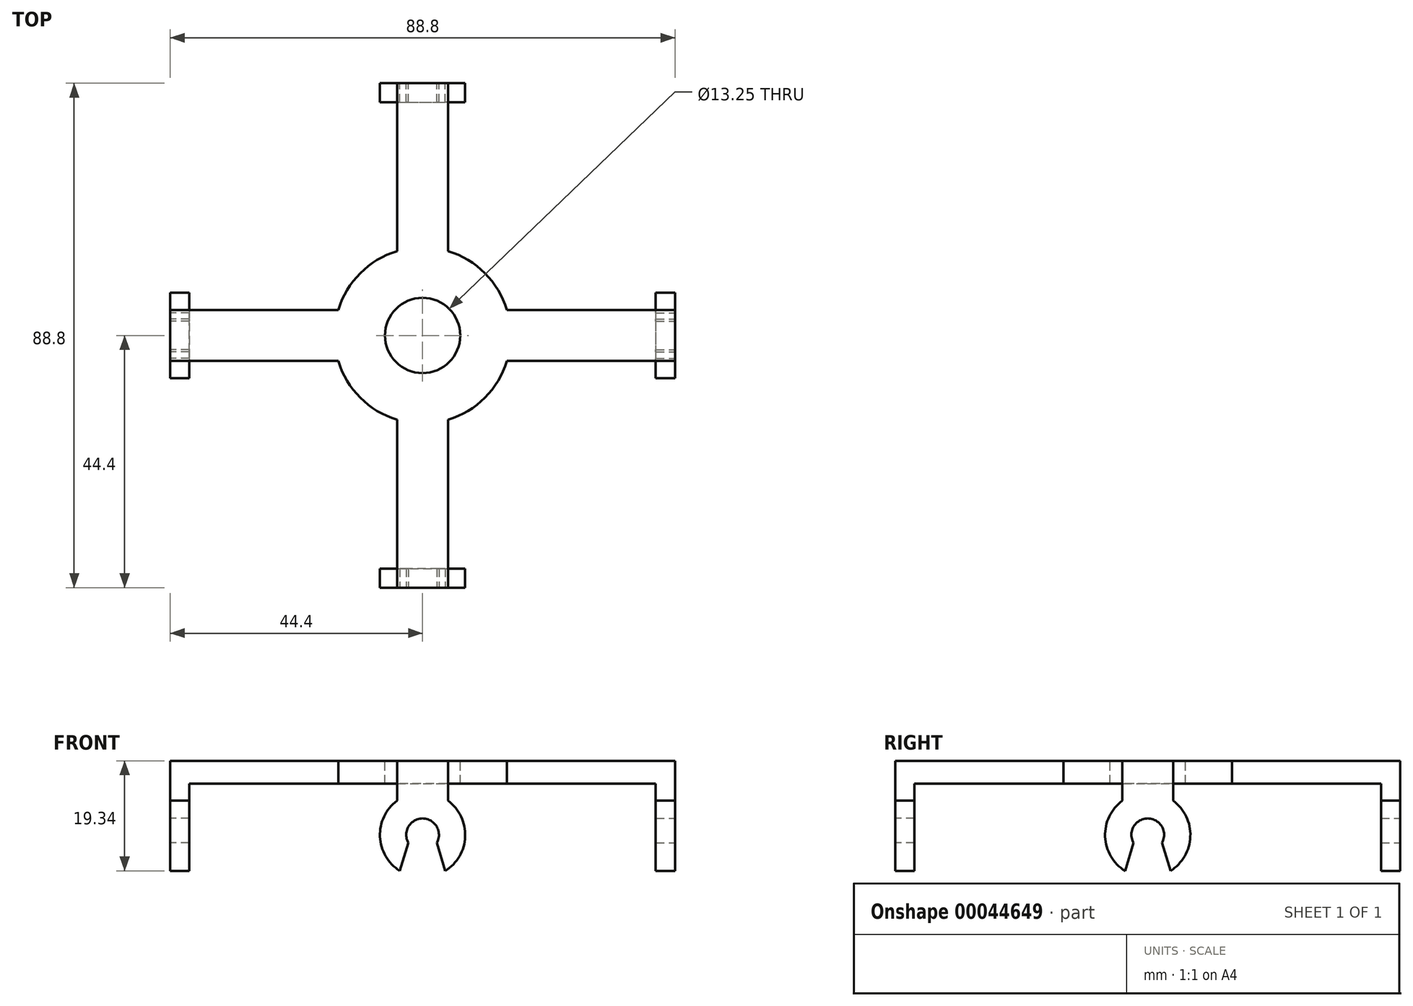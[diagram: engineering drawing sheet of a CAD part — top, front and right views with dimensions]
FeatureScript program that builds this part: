
annotation { "Feature Type Name" : "Feature", "Feature Type Description" : "" }
export const myFeature = defineFeature(function(context is Context, id is Id, definition is map)
    precondition{}
    {
        {
            var Q0;
            Q0=qCreatedBy(makeId("Top.planeOp"),FACE);
            var sketch = newSketch(context, id + "F0", { "sketchPlane" : qUnion([Q0])});
            skLineSegment(sketch, "E0.bottom", {"start": v(-44.4, 4.5) * mm, "end": v(44.4, 4.5) * mm});
            skLineSegment(sketch, "E0.top", {"start": v(-44.4, -4.5) * mm, "end": v(44.4, -4.5) * mm});
            skLineSegment(sketch, "E0.left", {"start": v(-44.4, 4.5) * mm, "end": v(-44.4, -4.5) * mm});
            skLineSegment(sketch, "E0.right", {"start": v(44.4, 4.5) * mm, "end": v(44.4, -4.5) * mm});
            skLineSegment(sketch, "E1.bottom", {"start": v(-4.5, 44.4) * mm, "end": v(4.5, 44.4) * mm});
            skLineSegment(sketch, "E1.top", {"start": v(-4.5, -44.4) * mm, "end": v(4.5, -44.4) * mm});
            skLineSegment(sketch, "E1.left", {"start": v(-4.5, 44.4) * mm, "end": v(-4.5, -44.4) * mm});
            skLineSegment(sketch, "E1.right", {"start": v(4.5, 44.4) * mm, "end": v(4.5, -44.4) * mm});
            skCircle(sketch, "E2", {"center": v(0, 0) * mm, "radius": 15.5 * mm});
            skSolve(sketch);
        }
        {
            var Q0;
            {var subQ0=sQuery(id+"F0.wireOp",EDGE,"E1.top");Q0=makeQuery(id+"F0.imprint","IMPRINT",FACE,{"disambiguationData":[TD([[makeQuery(id+"F0.imprint","IMPRINT",EDGE,{"derivedFrom":subQ0}),1.0]])]});}
            var Q1;
            {var subQ0=sQuery(id+"F0.wireOp",EDGE,"E1.left");var subQ1=sQuery(id+"F0.wireOp",EDGE,"E0.top");var subQ2=makeQuery(id+"F0.imprint","INTERSECT",VERTEX,{"derivedFrom":[subQ1,subQ0]});Q1=makeQuery(id+"F0.imprint","IMPRINT",FACE,{"disambiguationData":[TD([[makeQuery(id+"F0.imprint","IMPRINT",EDGE,{"disambiguationData":[TD([[subQ2,-1.0]])],"derivedFrom":subQ1}),-1.0]])]});}
            var Q2;
            {var subQ0=sQuery(id+"F0.wireOp",EDGE,"E2");var subQ1=sQuery(id+"F0.wireOp",EDGE,"E0.top");var subQ2=makeQuery(id+"F0.imprint","INTERSECT",VERTEX,{"disambiguationData":[OD(0.0)],"derivedFrom":[subQ1,subQ0]});Q2=makeQuery(id+"F0.imprint","IMPRINT",FACE,{"disambiguationData":[TD([[makeQuery(id+"F0.imprint","IMPRINT",EDGE,{"disambiguationData":[TD([[subQ2,-1.0]])],"derivedFrom":subQ1}),-1.0]])]});}
            var Q3;
            {var subQ0=sQuery(id+"F0.wireOp",EDGE,"E2");var subQ1=sQuery(id+"F0.wireOp",EDGE,"E0.bottom");var subQ2=makeQuery(id+"F0.imprint","INTERSECT",VERTEX,{"disambiguationData":[OD(0.0)],"derivedFrom":[subQ1,subQ0]});Q3=makeQuery(id+"F0.imprint","IMPRINT",FACE,{"disambiguationData":[TD([[makeQuery(id+"F0.imprint","IMPRINT",EDGE,{"disambiguationData":[TD([[subQ2,-1.0]])],"derivedFrom":subQ1}),-1.0]])]});}
            var Q4;
            {var subQ0=sQuery(id+"F0.wireOp",EDGE,"E2");var subQ1=sQuery(id+"F0.wireOp",EDGE,"E0.top");var subQ2=makeQuery(id+"F0.imprint","INTERSECT",VERTEX,{"disambiguationData":[OD(1.0)],"derivedFrom":[subQ1,subQ0]});Q4=makeQuery(id+"F0.imprint","IMPRINT",FACE,{"disambiguationData":[TD([[makeQuery(id+"F0.imprint","IMPRINT",EDGE,{"disambiguationData":[TD([[subQ2,1.0]])],"derivedFrom":subQ1}),-1.0]])]});}
            var Q5;
            {var subQ0=sQuery(id+"F0.wireOp",EDGE,"E2");var subQ1=sQuery(id+"F0.wireOp",EDGE,"E0.bottom");var subQ2=makeQuery(id+"F0.imprint","INTERSECT",VERTEX,{"disambiguationData":[OD(1.0)],"derivedFrom":[subQ1,subQ0]});Q5=makeQuery(id+"F0.imprint","IMPRINT",FACE,{"disambiguationData":[TD([[makeQuery(id+"F0.imprint","IMPRINT",EDGE,{"disambiguationData":[TD([[subQ2,1.0]])],"derivedFrom":subQ1}),-1.0]])]});}
            var Q6;
            {var subQ0=sQuery(id+"F0.wireOp",EDGE,"E0.right");Q6=makeQuery(id+"F0.imprint","IMPRINT",FACE,{"disambiguationData":[TD([[makeQuery(id+"F0.imprint","IMPRINT",EDGE,{"derivedFrom":subQ0}),-1.0]])]});}
            var Q7;
            {var subQ0=sQuery(id+"F0.wireOp",EDGE,"E0.left");Q7=makeQuery(id+"F0.imprint","IMPRINT",FACE,{"disambiguationData":[TD([[makeQuery(id+"F0.imprint","IMPRINT",EDGE,{"derivedFrom":subQ0}),1.0]])]});}
            var Q8;
            {var subQ0=sQuery(id+"F0.wireOp",EDGE,"E1.left");var subQ1=sQuery(id+"F0.wireOp",EDGE,"E0.bottom");var subQ2=makeQuery(id+"F0.imprint","INTERSECT",VERTEX,{"derivedFrom":[subQ1,subQ0]});Q8=makeQuery(id+"F0.imprint","IMPRINT",FACE,{"disambiguationData":[TD([[makeQuery(id+"F0.imprint","IMPRINT",EDGE,{"disambiguationData":[TD([[subQ2,-1.0]])],"derivedFrom":subQ1}),-1.0]])]});}
            var Q9;
            {var subQ0=sQuery(id+"F0.wireOp",EDGE,"E1.left");var subQ1=sQuery(id+"F0.wireOp",EDGE,"E0.bottom");var subQ2=makeQuery(id+"F0.imprint","INTERSECT",VERTEX,{"derivedFrom":[subQ1,subQ0]});Q9=makeQuery(id+"F0.imprint","IMPRINT",FACE,{"disambiguationData":[TD([[makeQuery(id+"F0.imprint","IMPRINT",EDGE,{"disambiguationData":[TD([[subQ2,-1.0]])],"derivedFrom":subQ1}),1.0]])]});}
            var Q10;
            {var subQ0=sQuery(id+"F0.wireOp",EDGE,"E2");var subQ1=sQuery(id+"F0.wireOp",EDGE,"E0.bottom");var subQ2=makeQuery(id+"F0.imprint","INTERSECT",VERTEX,{"disambiguationData":[OD(1.0)],"derivedFrom":[subQ1,subQ0]});Q10=makeQuery(id+"F0.imprint","IMPRINT",FACE,{"disambiguationData":[TD([[makeQuery(id+"F0.imprint","IMPRINT",EDGE,{"disambiguationData":[TD([[subQ2,1.0]])],"derivedFrom":subQ1}),1.0]])]});}
            var Q11;
            {var subQ0=sQuery(id+"F0.wireOp",EDGE,"E1.bottom");Q11=makeQuery(id+"F0.imprint","IMPRINT",FACE,{"disambiguationData":[TD([[makeQuery(id+"F0.imprint","IMPRINT",EDGE,{"derivedFrom":subQ0}),-1.0]])]});}
            var Q12;
            {var subQ0=sQuery(id+"F0.wireOp",EDGE,"E2");var subQ1=sQuery(id+"F0.wireOp",EDGE,"E0.bottom");var subQ2=makeQuery(id+"F0.imprint","INTERSECT",VERTEX,{"disambiguationData":[OD(0.0)],"derivedFrom":[subQ1,subQ0]});Q12=makeQuery(id+"F0.imprint","IMPRINT",FACE,{"disambiguationData":[TD([[makeQuery(id+"F0.imprint","IMPRINT",EDGE,{"disambiguationData":[TD([[subQ2,-1.0]])],"derivedFrom":subQ1}),1.0]])]});}
            var Q13;
            {var subQ0=sQuery(id+"F0.wireOp",EDGE,"E2");var subQ1=sQuery(id+"F0.wireOp",EDGE,"E1.left");var subQ2=makeQuery(id+"F0.imprint","INTERSECT",VERTEX,{"disambiguationData":[OD(0.0)],"derivedFrom":[subQ1,subQ0]});Q13=makeQuery(id+"F0.imprint","IMPRINT",FACE,{"disambiguationData":[TD([[makeQuery(id+"F0.imprint","IMPRINT",EDGE,{"disambiguationData":[TD([[subQ2,-1.0]])],"derivedFrom":subQ1}),-1.0]])]});}
            var Q14;
            {var subQ0=sQuery(id+"F0.wireOp",EDGE,"E2");var subQ1=sQuery(id+"F0.wireOp",EDGE,"E1.right");var subQ2=makeQuery(id+"F0.imprint","INTERSECT",VERTEX,{"disambiguationData":[OD(0.0)],"derivedFrom":[subQ1,subQ0]});Q14=makeQuery(id+"F0.imprint","IMPRINT",FACE,{"disambiguationData":[TD([[makeQuery(id+"F0.imprint","IMPRINT",EDGE,{"disambiguationData":[TD([[subQ2,-1.0]])],"derivedFrom":subQ1}),1.0]])]});}
            var Q15;
            {var subQ0=sQuery(id+"F0.wireOp",EDGE,"E1.right");var subQ1=sQuery(id+"F0.wireOp",EDGE,"E0.top");var subQ2=makeQuery(id+"F0.imprint","INTERSECT",VERTEX,{"derivedFrom":[subQ1,subQ0]});Q15=makeQuery(id+"F0.imprint","IMPRINT",FACE,{"disambiguationData":[TD([[makeQuery(id+"F0.imprint","IMPRINT",EDGE,{"disambiguationData":[TD([[subQ2,1.0]])],"derivedFrom":subQ1}),1.0]])]});}
            var Q16;
            {var subQ0=sQuery(id+"F0.wireOp",EDGE,"E1.left");var subQ1=sQuery(id+"F0.wireOp",EDGE,"E0.top");var subQ2=makeQuery(id+"F0.imprint","INTERSECT",VERTEX,{"derivedFrom":[subQ1,subQ0]});Q16=makeQuery(id+"F0.imprint","IMPRINT",FACE,{"disambiguationData":[TD([[makeQuery(id+"F0.imprint","IMPRINT",EDGE,{"disambiguationData":[TD([[subQ2,-1.0]])],"derivedFrom":subQ1}),1.0]])]});}
            var Q17;
            {var subQ0=sQuery(id+"F0.wireOp",EDGE,"E1.right");var subQ1=sQuery(id+"F0.wireOp",EDGE,"E0.bottom");var subQ2=makeQuery(id+"F0.imprint","INTERSECT",VERTEX,{"derivedFrom":[subQ1,subQ0]});Q17=makeQuery(id+"F0.imprint","IMPRINT",FACE,{"disambiguationData":[TD([[makeQuery(id+"F0.imprint","IMPRINT",EDGE,{"disambiguationData":[TD([[subQ2,1.0]])],"derivedFrom":subQ1}),-1.0]])]});}
            extrude(context, id + "F1", {"entities" : qUnion([Q0, Q1, Q2, Q3, Q4, Q5, Q6, Q7, Q8, Q9, Q10, Q11, Q12, Q13, Q14, Q15, Q16, Q17]), "depth" : 4 * mm});
        }
        {
            var Q0;
            Q0=makeQuery(id+"F1.opExtrude","CAP_FACE",FACE,{"disambiguationData":[OSD([sQuery(id+"F0.wireOp",EDGE,"E0.bottom"),sQuery(id+"F0.wireOp",EDGE,"E0.top"),sQuery(id+"F0.wireOp",EDGE,"E0.left"),sQuery(id+"F0.wireOp",EDGE,"E0.right"),sQuery(id+"F0.wireOp",EDGE,"E1.bottom"),sQuery(id+"F0.wireOp",EDGE,"E1.top"),sQuery(id+"F0.wireOp",EDGE,"E1.left"),sQuery(id+"F0.wireOp",EDGE,"E1.right"),sQuery(id+"F0.wireOp",EDGE,"E2")])],"isStart":true});
            var sketch = newSketch(context, id + "F2", { "sketchPlane" : qUnion([Q0])});
            skPoint(sketch, "E3", {"position": v(0, 0) * mm});
            skSolve(sketch);
        }
        {
            var Q0;
            Q0=makeQuery(id+"F1.opExtrude","SWEPT_FACE",FACE,{"disambiguationData":[OSD([sQuery(id+"F0.wireOp",EDGE,"E1.top")])]});
            var sketch = newSketch(context, id + "F3", { "sketchPlane" : qUnion([Q0])});
            skLineSegment(sketch, "E4.bottom", {"start": v(-4.5, 0) * mm, "end": v(4.5, 0) * mm});
            skLineSegment(sketch, "E4.top", {"start": v(-4.5, -3) * mm, "end": v(4.5, -3) * mm});
            skLineSegment(sketch, "E4.left", {"start": v(-4.5, 0) * mm, "end": v(-4.5, -3) * mm});
            skLineSegment(sketch, "E4.right", {"start": v(4.5, 0) * mm, "end": v(4.5, -3) * mm});
            skCircle(sketch, "E5", {"center": v(0, -9) * mm, "radius": 7.5 * mm});
            skPoint(sketch, "E5.centerSnap0", {"position": v(0, -3) * mm});
            skCircle(sketch, "E6", {"center": v(0, -9) * mm, "radius": 2.88 * mm});
            skLineSegment(sketch, "E7", {"start": v(-2.5, -10.42) * mm, "end": v(-4, -15.34) * mm});
            skLineSegment(sketch, "E8", {"start": v(-4, -15.34) * mm, "end": v(4, -15.34) * mm});
            skLineSegment(sketch, "E9", {"start": v(4, -15.34) * mm, "end": v(2.5, -10.42) * mm});
            skLineSegment(sketch, "E10", {"start": v(2.5, -10.42) * mm, "end": v(-2.5, -10.42) * mm});
            skSolve(sketch);
        }
        {
            var Q0;
            Q0=makeQuery(id+"F1.opExtrude","SWEPT_FACE",FACE,{"disambiguationData":[OSD([sQuery(id+"F0.wireOp",EDGE,"E0.left")])]});
            var sketch = newSketch(context, id + "F4", { "sketchPlane" : qUnion([Q0])});
            skLineSegment(sketch, "E11.bottom", {"start": v(-4.5, 0) * mm, "end": v(4.5, 0) * mm});
            skLineSegment(sketch, "E11.top", {"start": v(-4.5, -3) * mm, "end": v(4.5, -3) * mm});
            skLineSegment(sketch, "E11.left", {"start": v(-4.5, 0) * mm, "end": v(-4.5, -3) * mm});
            skLineSegment(sketch, "E11.right", {"start": v(4.5, 0) * mm, "end": v(4.5, -3) * mm});
            skCircle(sketch, "E12", {"center": v(0, -9) * mm, "radius": 7.5 * mm});
            skPoint(sketch, "E12.centerSnap0", {"position": v(0, -3) * mm});
            skCircle(sketch, "E13", {"center": v(0, -9) * mm, "radius": 2.88 * mm});
            skLineSegment(sketch, "E14", {"start": v(-2.5, -10.42) * mm, "end": v(-4, -15.34) * mm});
            skLineSegment(sketch, "E15", {"start": v(-4, -15.34) * mm, "end": v(4, -15.34) * mm});
            skLineSegment(sketch, "E16", {"start": v(4, -15.34) * mm, "end": v(2.5, -10.42) * mm});
            skLineSegment(sketch, "E17", {"start": v(2.5, -10.42) * mm, "end": v(-2.5, -10.42) * mm});
            skSolve(sketch);
        }
        {
            var Q0;
            Q0=makeQuery(id+"F1.opExtrude","SWEPT_FACE",FACE,{"disambiguationData":[OSD([sQuery(id+"F0.wireOp",EDGE,"E1.bottom")])]});
            var sketch = newSketch(context, id + "F5", { "sketchPlane" : qUnion([Q0])});
            skLineSegment(sketch, "E18.bottom", {"start": v(-4.5, 0) * mm, "end": v(4.5, 0) * mm});
            skLineSegment(sketch, "E18.top", {"start": v(-4.5, -3) * mm, "end": v(4.5, -3) * mm});
            skLineSegment(sketch, "E18.left", {"start": v(-4.5, 0) * mm, "end": v(-4.5, -3) * mm});
            skLineSegment(sketch, "E18.right", {"start": v(4.5, 0) * mm, "end": v(4.5, -3) * mm});
            skCircle(sketch, "E19", {"center": v(0, -9) * mm, "radius": 7.5 * mm});
            skPoint(sketch, "E19.centerSnap0", {"position": v(0, -3) * mm});
            skCircle(sketch, "E20", {"center": v(0, -9) * mm, "radius": 2.88 * mm});
            skLineSegment(sketch, "E21", {"start": v(-2.5, -10.42) * mm, "end": v(-4, -15.34) * mm});
            skLineSegment(sketch, "E22", {"start": v(-4, -15.34) * mm, "end": v(4, -15.34) * mm});
            skLineSegment(sketch, "E23", {"start": v(4, -15.34) * mm, "end": v(2.5, -10.42) * mm});
            skLineSegment(sketch, "E24", {"start": v(2.5, -10.42) * mm, "end": v(-2.5, -10.42) * mm});
            skSolve(sketch);
        }
        {
            var Q0;
            Q0=makeQuery(id+"F1.opExtrude","SWEPT_FACE",FACE,{"disambiguationData":[OSD([sQuery(id+"F0.wireOp",EDGE,"E0.right")])]});
            var sketch = newSketch(context, id + "F6", { "sketchPlane" : qUnion([Q0])});
            skLineSegment(sketch, "E25.bottom", {"start": v(-4.5, 0) * mm, "end": v(4.5, 0) * mm});
            skLineSegment(sketch, "E25.top", {"start": v(-4.5, -3) * mm, "end": v(4.5, -3) * mm});
            skLineSegment(sketch, "E25.left", {"start": v(-4.5, 0) * mm, "end": v(-4.5, -3) * mm});
            skLineSegment(sketch, "E25.right", {"start": v(4.5, 0) * mm, "end": v(4.5, -3) * mm});
            skCircle(sketch, "E26", {"center": v(0, -9) * mm, "radius": 7.5 * mm});
            skPoint(sketch, "E26.centerSnap0", {"position": v(0, -3) * mm});
            skCircle(sketch, "E27", {"center": v(0, -9) * mm, "radius": 2.88 * mm});
            skLineSegment(sketch, "E28", {"start": v(-2.5, -10.42) * mm, "end": v(-4, -15.34) * mm});
            skLineSegment(sketch, "E29", {"start": v(-4, -15.34) * mm, "end": v(4, -15.34) * mm});
            skLineSegment(sketch, "E30", {"start": v(4, -15.34) * mm, "end": v(2.5, -10.42) * mm});
            skLineSegment(sketch, "E31", {"start": v(2.5, -10.42) * mm, "end": v(-2.5, -10.42) * mm});
            skSolve(sketch);
        }
        {
            var Q0;
            Q0=makeQuery(id+"F3.imprint","IMPRINT",FACE,{"disambiguationData":[TD([[makeQuery(id+"F3.imprint","IMPRINT",EDGE,{"derivedFrom":sQuery(id+"F3.wireOp",EDGE,"E4.bottom")}),-1.0]])]});
            var Q1;
            {var subQ5=sQuery(id+"F3.wireOp",EDGE,"E4.top");Q1=makeQuery(id+"F3.imprint","IMPRINT",FACE,{"disambiguationData":[TD([[makeQuery(id+"F3.imprint","IMPRINT",EDGE,{"derivedFrom":subQ5}),-1.0]])]});}
            var Q2;
            {var subQ0=sQuery(id+"F3.wireOp",EDGE,"E4.top");Q2=makeQuery(id+"F3.imprint","IMPRINT",FACE,{"disambiguationData":[TD([[makeQuery(id+"F3.imprint","IMPRINT",EDGE,{"derivedFrom":subQ0}),1.0]])]});}
            extrude(context, id + "F7", {"entities" : qUnion([Q0, Q1, Q2]), "operationType" : NewBodyOperationType.ADD, "oppositeDirection" : true, "depth" : 3.38 * mm});
        }
        {
            var Q0;
            Q0=makeQuery(id+"F6.imprint","IMPRINT",FACE,{"disambiguationData":[TD([[makeQuery(id+"F6.imprint","IMPRINT",EDGE,{"derivedFrom":sQuery(id+"F6.wireOp",EDGE,"E25.bottom")}),1.0]])]});
            var Q1;
            {var subQ0=sQuery(id+"F6.wireOp",EDGE,"E25.top");Q1=makeQuery(id+"F6.imprint","IMPRINT",FACE,{"disambiguationData":[TD([[makeQuery(id+"F6.imprint","IMPRINT",EDGE,{"derivedFrom":subQ0}),1.0]])]});}
            var Q2;
            {var subQ1=sQuery(id+"F6.wireOp",EDGE,"E25.top");Q2=makeQuery(id+"F6.imprint","IMPRINT",FACE,{"disambiguationData":[TD([[makeQuery(id+"F6.imprint","IMPRINT",EDGE,{"derivedFrom":subQ1}),-1.0]])]});}
            extrude(context, id + "F8", {"entities" : qUnion([Q0, Q1, Q2]), "operationType" : NewBodyOperationType.ADD, "oppositeDirection" : true, "depth" : 3.38 * mm});
        }
        {
            var Q0;
            Q0=makeQuery(id+"F5.imprint","IMPRINT",FACE,{"disambiguationData":[TD([[makeQuery(id+"F5.imprint","IMPRINT",EDGE,{"derivedFrom":sQuery(id+"F5.wireOp",EDGE,"E18.bottom")}),1.0]])]});
            var Q1;
            {var subQ0=sQuery(id+"F5.wireOp",EDGE,"E18.top");Q1=makeQuery(id+"F5.imprint","IMPRINT",FACE,{"disambiguationData":[TD([[makeQuery(id+"F5.imprint","IMPRINT",EDGE,{"derivedFrom":subQ0}),1.0]])]});}
            var Q2;
            {var subQ5=sQuery(id+"F5.wireOp",EDGE,"E18.top");Q2=makeQuery(id+"F5.imprint","IMPRINT",FACE,{"disambiguationData":[TD([[makeQuery(id+"F5.imprint","IMPRINT",EDGE,{"derivedFrom":subQ5}),-1.0]])]});}
            extrude(context, id + "F9", {"entities" : qUnion([Q0, Q1, Q2]), "operationType" : NewBodyOperationType.ADD, "oppositeDirection" : true, "depth" : 3.38 * mm});
        }
        {
            var Q0;
            Q0=makeQuery(id+"F4.imprint","IMPRINT",FACE,{"disambiguationData":[TD([[makeQuery(id+"F4.imprint","IMPRINT",EDGE,{"derivedFrom":sQuery(id+"F4.wireOp",EDGE,"E11.bottom")}),-1.0]])]});
            var Q1;
            {var subQ1=sQuery(id+"F4.wireOp",EDGE,"E11.top");Q1=makeQuery(id+"F4.imprint","IMPRINT",FACE,{"disambiguationData":[TD([[makeQuery(id+"F4.imprint","IMPRINT",EDGE,{"derivedFrom":subQ1}),-1.0]])]});}
            var Q2;
            {var subQ0=sQuery(id+"F4.wireOp",EDGE,"E11.top");Q2=makeQuery(id+"F4.imprint","IMPRINT",FACE,{"disambiguationData":[TD([[makeQuery(id+"F4.imprint","IMPRINT",EDGE,{"derivedFrom":subQ0}),1.0]])]});}
            extrude(context, id + "F10", {"entities" : qUnion([Q0, Q1, Q2]), "operationType" : NewBodyOperationType.ADD, "oppositeDirection" : true, "depth" : 3.38 * mm});
        }
        {
            var Q0;
            Q0=sQuery(id+"F2.wireOp",VERTEX,"E3");
            var Q1;
            Q1=makeQuery(id+"F1.opExtrude","SWEPT_BODY",BODY,{"disambiguationData":[OSD([sQuery(id+"F0.wireOp",EDGE,"E0.bottom"),sQuery(id+"F0.wireOp",EDGE,"E0.top"),sQuery(id+"F0.wireOp",EDGE,"E0.left"),sQuery(id+"F0.wireOp",EDGE,"E0.right"),sQuery(id+"F0.wireOp",EDGE,"E1.bottom"),sQuery(id+"F0.wireOp",EDGE,"E1.top"),sQuery(id+"F0.wireOp",EDGE,"E1.left"),sQuery(id+"F0.wireOp",EDGE,"E1.right"),sQuery(id+"F0.wireOp",EDGE,"E2")])]});
            hole(context, id + "F11", {"style" : HoleStyle.SIMPLE, "holeDiameter" : 13.25 * mm, "endStyle" : HoleEndStyle.THROUGH, "locations" : qUnion([Q0]), "scope" : qUnion([Q1])});
        }
    });
